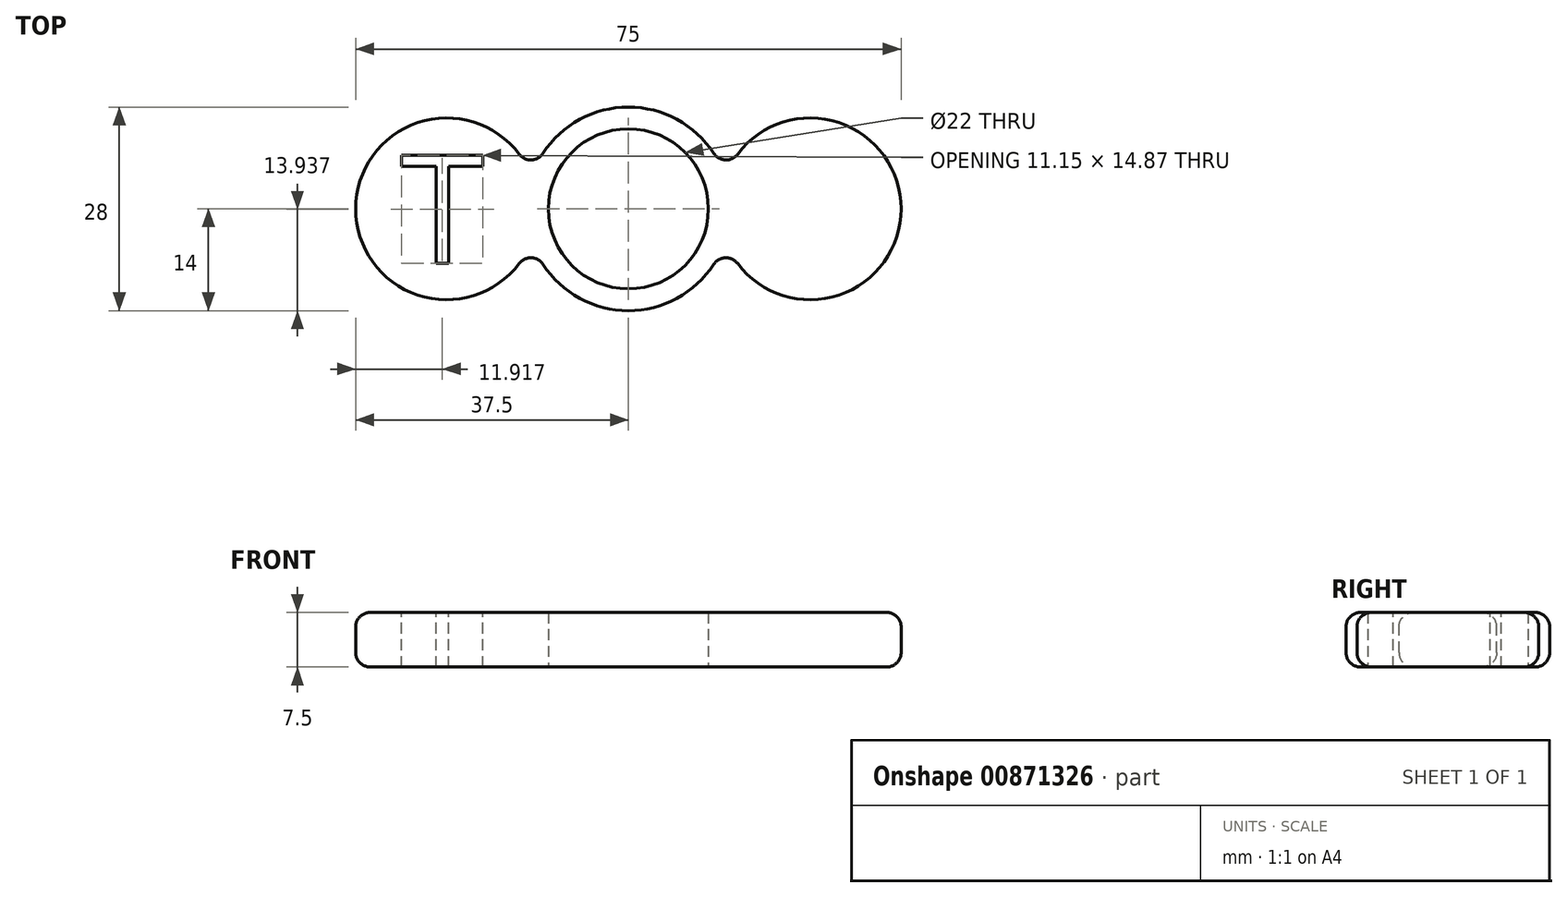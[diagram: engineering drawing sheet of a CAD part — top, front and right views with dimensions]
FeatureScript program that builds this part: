
annotation { "Feature Type Name" : "Feature", "Feature Type Description" : "" }
export const myFeature = defineFeature(function(context is Context, id is Id, definition is map)
    precondition{}
    {
        {
            var Q0;
            Q0=qCreatedBy(makeId("Top.planeOp"),FACE);
            var sketch = newSketch(context, id + "F0", { "sketchPlane" : qUnion([Q0])});
            skArc(sketch, "E0", {"start": v(-13.3, -4.39) * mm, "mid": v(0, -14) * mm, "end": v(13.3, -4.39) * mm});
            skCircle(sketch, "E1", {"center": v(0, 0) * mm, "radius": 11 * mm});
            skArc(sketch, "E2", {"start": v(-13.3, 4.39) * mm, "mid": v(-37.5, 0) * mm, "end": v(-13.3, -4.39) * mm});
            skArc(sketch, "E3.MirrorCS", {"start": v(13.3, 4.39) * mm, "mid": v(37.5, 0) * mm, "end": v(13.3, -4.39) * mm});
            skArc(sketch, "E4.trimOffspring", {"start": v(13.3, 4.39) * mm, "mid": v(0, 14) * mm, "end": v(-13.3, 4.39) * mm});
            skSolve(sketch);
        }
        {
            var Q0;
            Q0=makeQuery(id+"F0.imprint","IMPRINT",FACE,{"disambiguationData":[TD([[makeQuery(id+"F0.imprint","IMPRINT",EDGE,{"derivedFrom":sQuery(id+"F0.wireOp",EDGE,"E0")}),1.0]])]});
            extrude(context, id + "F1", {"entities" : qUnion([Q0]), "depth" : 7.5 * mm, "offsetDistance" : 25 * mm});
        }
        {
            var Q0;
            Q0=makeQuery(id+"F1.opExtrude","SWEPT_EDGE",EDGE,{"disambiguationData":[OSD([sQuery(id+"F0.wireOp",EDGE,"E0"),sQuery(id+"F0.wireOp",EDGE,"E2")])]});
            var Q1;
            Q1=makeQuery(id+"F1.opExtrude","SWEPT_EDGE",EDGE,{"disambiguationData":[OSD([sQuery(id+"F0.wireOp",EDGE,"E0"),sQuery(id+"F0.wireOp",EDGE,"E3.MirrorCS")])]});
            var Q2;
            Q2=makeQuery(id+"F1.opExtrude","SWEPT_EDGE",EDGE,{"disambiguationData":[OSD([sQuery(id+"F0.wireOp",EDGE,"E3.MirrorCS"),sQuery(id+"F0.wireOp",EDGE,"E4.trimOffspring")])]});
            var Q3;
            Q3=makeQuery(id+"F1.opExtrude","SWEPT_EDGE",EDGE,{"disambiguationData":[OSD([sQuery(id+"F0.wireOp",EDGE,"E2"),sQuery(id+"F0.wireOp",EDGE,"E4.trimOffspring")])]});
            fillet(context, id + "F2", {"entities" : qUnion([Q0, Q1, Q2, Q3]), "radius" : 2 * mm, "tangentPropagation" : true, "allowEdgeOverflow" : false});
        }
        {
            var Q0;
            Q0=makeQuery(id+"F1.opExtrude","CAP_EDGE",EDGE,{"disambiguationData":[OSD([sQuery(id+"F0.wireOp",EDGE,"E2")])],"isStart":false});
            var Q1;
            Q1=makeQuery(id+"F1.opExtrude","CAP_EDGE",EDGE,{"disambiguationData":[OSD([sQuery(id+"F0.wireOp",EDGE,"E2")])],"isStart":true});
            fillet(context, id + "F3", {"entities" : qUnion([Q0, Q1]), "radius" : 2 * mm, "tangentPropagation" : true, "allowEdgeOverflow" : false});
        }
        {
            var Q0;
            Q0=makeQuery(id+"F1.opExtrude","CAP_FACE",FACE,{"disambiguationData":[OSD([sQuery(id+"F0.wireOp",EDGE,"E0"),sQuery(id+"F0.wireOp",EDGE,"E1"),sQuery(id+"F0.wireOp",EDGE,"E2"),sQuery(id+"F0.wireOp",EDGE,"E3.MirrorCS"),sQuery(id+"F0.wireOp",EDGE,"E4.trimOffspring")])],"isStart":false});
            var sketch = newSketch(context, id + "F4", { "sketchPlane" : qUnion([Q0])});
            skText(sketch, "E5", { "text": "T", "fontName": "OpenSans-Regular.ttf"});
            const initialGuessF4  = {"E5": [-0.03134, -0.0075, 1, 0, 0.015]};
            skSetInitialGuess(sketch, initialGuessF4);
            skSolve(sketch);
        }
        {
            var Q0;
            Q0 = qSketchRegion(id + "F4", true);
            extrude(context, id + "F5", {"entities" : qUnion([Q0]), "operationType" : NewBodyOperationType.REMOVE, "oppositeDirection" : true, "depth" : 25 * mm, "offsetDistance" : 25 * mm});
        }
    });
